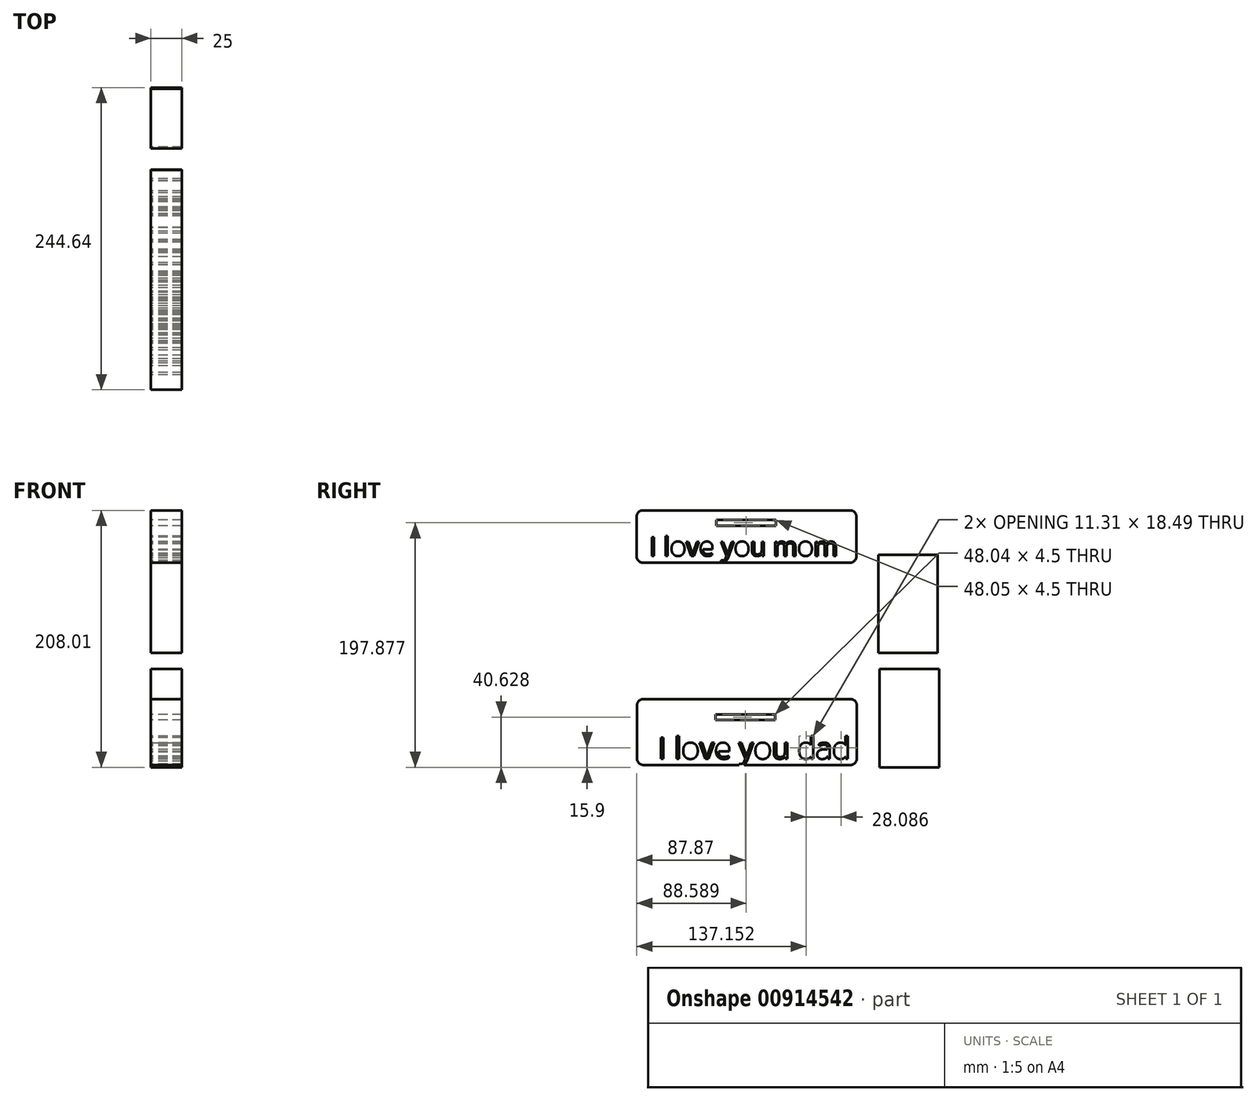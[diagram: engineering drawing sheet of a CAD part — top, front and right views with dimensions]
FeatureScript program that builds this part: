
annotation { "Feature Type Name" : "Feature", "Feature Type Description" : "" }
export const myFeature = defineFeature(function(context is Context, id is Id, definition is map)
    precondition{}
    {
        {
            var Q0;
            Q0=qCreatedBy(makeId("Right.planeOp"),FACE);
            var sketch = newSketch(context, id + "F0", { "sketchPlane" : qUnion([Q0])});
            skLineSegment(sketch, "E0", {"start": v(-72.6, 69.5) * mm, "end": v(66.76, 69.5) * mm});
            skLineSegment(sketch, "E1", {"start": v(71.76, 64.5) * mm, "end": v(71.76, 32.1) * mm});
            skLineSegment(sketch, "E2", {"start": v(66.76, 27.1) * mm, "end": v(-101.04, 27.1) * mm});
            skLineSegment(sketch, "E3", {"start": v(-106.04, 32.1) * mm, "end": v(-106.04, 64.5) * mm});
            skLineSegment(sketch, "E4", {"start": v(-101.04, 69.5) * mm, "end": v(-72.6, 69.5) * mm});
            skText(sketch, "E5", { "text": "I love you mom", "fontName": "OpenSans-Regular.ttf"});
            skLineSegment(sketch, "E6", {"start": v(89.45, 33.47) * mm, "end": v(137.5, 33.47) * mm});
            skLineSegment(sketch, "E7", {"start": v(137.5, 33.47) * mm, "end": v(137.5, -45.98) * mm});
            skLineSegment(sketch, "E8", {"start": v(137.5, -45.98) * mm, "end": v(89.45, -45.98) * mm});
            skLineSegment(sketch, "E9", {"start": v(89.45, -45.98) * mm, "end": v(89.45, 33.47) * mm});
            skPoint(sketch, "E10", {"position": v(-0.42, 69.5) * mm});
            skLineSegment(sketch, "E11", {"start": v(-41.47, 61.6) * mm, "end": v(6.57, 61.6) * mm});
            skLineSegment(sketch, "E12", {"start": v(6.57, 61.6) * mm, "end": v(6.57, 57.1) * mm});
            skLineSegment(sketch, "E13", {"start": v(6.57, 57.1) * mm, "end": v(-41.47, 57.1) * mm});
            skLineSegment(sketch, "E14", {"start": v(-41.47, 57.1) * mm, "end": v(-41.47, 61.6) * mm});
            skLineSegment(sketch, "E15", {"start": v(-106.17, -6.45) * mm, "end": v(-106.17, -6.45) * mm});
            skPoint(sketch, "E16.visualSharp", {"position": v(-106.04, 27.1) * mm});
            skArc(sketch, "E16.filletArc", {"start": v(-106.04, 32.1) * mm, "mid": v(-104.58, 28.57) * mm, "end": v(-101.04, 27.1) * mm});
            skPoint(sketch, "E17.visualSharp", {"position": v(71.76, 27.1) * mm});
            skArc(sketch, "E17.filletArc", {"start": v(66.76, 27.1) * mm, "mid": v(70.3, 28.57) * mm, "end": v(71.76, 32.1) * mm});
            skPoint(sketch, "E18.visualSharp", {"position": v(71.76, 69.5) * mm});
            skArc(sketch, "E18.filletArc", {"start": v(71.76, 64.5) * mm, "mid": v(70.3, 68.03) * mm, "end": v(66.76, 69.5) * mm});
            skPoint(sketch, "E19.visualSharp", {"position": v(-106.04, 69.5) * mm});
            skArc(sketch, "E19.filletArc", {"start": v(-101.04, 69.5) * mm, "mid": v(-104.58, 68.03) * mm, "end": v(-106.04, 64.5) * mm});
            skLineSegment(sketch, "E20", {"start": v(-105.73, -88.3) * mm, "end": v(-105.73, -131.63) * mm});
            skLineSegment(sketch, "E21", {"start": v(-100.73, -136.63) * mm, "end": v(67.07, -136.63) * mm});
            skLineSegment(sketch, "E22", {"start": v(72.07, -131.63) * mm, "end": v(72.07, -88.3) * mm});
            skLineSegment(sketch, "E23", {"start": v(67.07, -83.3) * mm, "end": v(-100.73, -83.3) * mm});
            skPoint(sketch, "E24.visualSharp", {"position": v(-105.73, -83.3) * mm});
            skArc(sketch, "E24.filletArc", {"start": v(-100.73, -83.3) * mm, "mid": v(-104.26, -84.75) * mm, "end": v(-105.73, -88.3) * mm});
            skPoint(sketch, "E25.visualSharp", {"position": v(-105.73, -136.63) * mm});
            skArc(sketch, "E25.filletArc", {"start": v(-105.73, -131.63) * mm, "mid": v(-104.26, -135.17) * mm, "end": v(-100.73, -136.63) * mm});
            skPoint(sketch, "E26.visualSharp", {"position": v(72.07, -136.63) * mm});
            skArc(sketch, "E26.filletArc", {"start": v(67.07, -136.63) * mm, "mid": v(70.6, -135.17) * mm, "end": v(72.07, -131.63) * mm});
            skPoint(sketch, "E27.visualSharp", {"position": v(72.07, -83.3) * mm});
            skArc(sketch, "E27.filletArc", {"start": v(72.07, -88.3) * mm, "mid": v(70.6, -84.75) * mm, "end": v(67.07, -83.3) * mm});
            skLineSegment(sketch, "E28", {"start": v(-42.2, -95.64) * mm, "end": v(-42.2, -100.14) * mm});
            skLineSegment(sketch, "E29", {"start": v(-42.2, -100.14) * mm, "end": v(5.85, -100.14) * mm});
            skLineSegment(sketch, "E30", {"start": v(5.85, -100.14) * mm, "end": v(5.85, -95.85) * mm});
            skLineSegment(sketch, "E31", {"start": v(5.85, -95.85) * mm, "end": v(-42.2, -95.64) * mm});
            skText(sketch, "E32", { "text": "I love you dad\n", "fontName": "OpenSans-Regular.ttf"});
            skLineSegment(sketch, "E33", {"start": v(90.56, -59.07) * mm, "end": v(90.56, -138.52) * mm});
            skLineSegment(sketch, "E34", {"start": v(90.56, -138.52) * mm, "end": v(138.6, -138.52) * mm});
            skLineSegment(sketch, "E35", {"start": v(138.6, -138.52) * mm, "end": v(138.6, -59.07) * mm});
            skLineSegment(sketch, "E36", {"start": v(138.6, -59.07) * mm, "end": v(90.56, -59.07) * mm});
            const initialGuessF0  = {"E5": [-0.09593, 0.03263, 1, 0, 0.01535], "E32": [-0.0888, -0.13163, 1, 0, 0.0173]};
            skSetInitialGuess(sketch, initialGuessF0);
            skSolve(sketch);
        }
        {
            var Q0;
            Q0=makeQuery(id+"F0.imprint","IMPRINT",FACE,{"disambiguationData":[TD([[makeQuery(id+"F0.imprint","IMPRINT",EDGE,{"derivedFrom":sQuery(id+"F0.wireOp",EDGE,"E6")}),-1.0]])]});
            var Q1;
            Q1=makeQuery(id+"F0.imprint","IMPRINT",FACE,{"disambiguationData":[TD([[makeQuery(id+"F0.imprint","IMPRINT",EDGE,{"derivedFrom":sQuery(id+"F0.wireOp",EDGE,"E20")}),1.0]])]});
            extrude(context, id + "F1", {"entities" : qUnion([Q0, Q1]), "depth" : 25 * mm, "offsetDistance" : 25 * mm});
        }
        {
            var Q0;
            Q0 = qSketchRegion(id + "F0", true);
            extrude(context, id + "F2", {"entities" : qUnion([Q0]), "depth" : 25 * mm, "offsetDistance" : 25 * mm});
        }
        {
            var Q0;
            Q0=makeQuery(id+"F2.opExtrude","SWEPT_BODY",BODY,{"disambiguationData":[OSD([sQuery(id+"F0.wireOp",EDGE,"E20"),sQuery(id+"F0.wireOp",EDGE,"E21"),sQuery(id+"F0.wireOp",EDGE,"E22"),sQuery(id+"F0.wireOp",EDGE,"E23"),sQuery(id+"F0.wireOp",EDGE,"E24.filletArc"),sQuery(id+"F0.wireOp",EDGE,"E25.filletArc"),sQuery(id+"F0.wireOp",EDGE,"E26.filletArc"),sQuery(id+"F0.wireOp",EDGE,"E27.filletArc"),sQuery(id+"F0.wireOp",EDGE,"E28"),sQuery(id+"F0.wireOp",EDGE,"E29"),sQuery(id+"F0.wireOp",EDGE,"E30"),sQuery(id+"F0.wireOp",EDGE,"E31"),sQuery(id+"F0.wireOp",EDGE,"E32.sketch_text.stroke-0"),sQuery(id+"F0.wireOp",EDGE,"E32.sketch_text.stroke-1"),sQuery(id+"F0.wireOp",EDGE,"E32.sketch_text.stroke-2"),sQuery(id+"F0.wireOp",EDGE,"E32.sketch_text.stroke-3"),sQuery(id+"F0.wireOp",EDGE,"E32.sketch_text.stroke-4"),sQuery(id+"F0.wireOp",EDGE,"E32.sketch_text.stroke-5"),sQuery(id+"F0.wireOp",EDGE,"E32.sketch_text.stroke-6"),sQuery(id+"F0.wireOp",EDGE,"E32.sketch_text.stroke-7"),sQuery(id+"F0.wireOp",EDGE,"E32.sketch_text.stroke-8"),sQuery(id+"F0.wireOp",EDGE,"E32.sketch_text.stroke-9"),sQuery(id+"F0.wireOp",EDGE,"E32.sketch_text.stroke-10"),sQuery(id+"F0.wireOp",EDGE,"E32.sketch_text.stroke-11"),sQuery(id+"F0.wireOp",EDGE,"E32.sketch_text.stroke-12"),sQuery(id+"F0.wireOp",EDGE,"E32.sketch_text.stroke-13"),sQuery(id+"F0.wireOp",EDGE,"E32.sketch_text.stroke-14"),sQuery(id+"F0.wireOp",EDGE,"E32.sketch_text.stroke-15"),sQuery(id+"F0.wireOp",EDGE,"E32.sketch_text.stroke-16"),sQuery(id+"F0.wireOp",EDGE,"E32.sketch_text.stroke-25"),sQuery(id+"F0.wireOp",EDGE,"E32.sketch_text.stroke-26"),sQuery(id+"F0.wireOp",EDGE,"E32.sketch_text.stroke-27"),sQuery(id+"F0.wireOp",EDGE,"E32.sketch_text.stroke-28"),sQuery(id+"F0.wireOp",EDGE,"E32.sketch_text.stroke-29"),sQuery(id+"F0.wireOp",EDGE,"E32.sketch_text.stroke-30"),sQuery(id+"F0.wireOp",EDGE,"E32.sketch_text.stroke-31"),sQuery(id+"F0.wireOp",EDGE,"E32.sketch_text.stroke-32"),sQuery(id+"F0.wireOp",EDGE,"E32.sketch_text.stroke-33"),sQuery(id+"F0.wireOp",EDGE,"E32.sketch_text.stroke-34"),sQuery(id+"F0.wireOp",EDGE,"E32.sketch_text.stroke-35"),sQuery(id+"F0.wireOp",EDGE,"E32.sketch_text.stroke-36"),sQuery(id+"F0.wireOp",EDGE,"E32.sketch_text.stroke-37"),sQuery(id+"F0.wireOp",EDGE,"E32.sketch_text.stroke-38"),sQuery(id+"F0.wireOp",EDGE,"E32.sketch_text.stroke-39"),sQuery(id+"F0.wireOp",EDGE,"E32.sketch_text.stroke-40"),sQuery(id+"F0.wireOp",EDGE,"E32.sketch_text.stroke-41"),sQuery(id+"F0.wireOp",EDGE,"E32.sketch_text.stroke-42"),sQuery(id+"F0.wireOp",EDGE,"E32.sketch_text.stroke-43"),sQuery(id+"F0.wireOp",EDGE,"E32.sketch_text.stroke-44"),sQuery(id+"F0.wireOp",EDGE,"E32.sketch_text.stroke-45"),sQuery(id+"F0.wireOp",EDGE,"E32.sketch_text.stroke-46"),sQuery(id+"F0.wireOp",EDGE,"E32.sketch_text.stroke-47"),sQuery(id+"F0.wireOp",EDGE,"E32.sketch_text.stroke-48"),sQuery(id+"F0.wireOp",EDGE,"E32.sketch_text.stroke-63"),sQuery(id+"F0.wireOp",EDGE,"E32.sketch_text.stroke-64"),sQuery(id+"F0.wireOp",EDGE,"E32.sketch_text.stroke-65"),sQuery(id+"F0.wireOp",EDGE,"E32.sketch_text.stroke-70"),sQuery(id+"F0.wireOp",EDGE,"E32.sketch_text.stroke-71"),sQuery(id+"F0.wireOp",EDGE,"E32.sketch_text.stroke-72"),sQuery(id+"F0.wireOp",EDGE,"E32.sketch_text.stroke-73"),sQuery(id+"F0.wireOp",EDGE,"E32.sketch_text.stroke-74"),sQuery(id+"F0.wireOp",EDGE,"E32.sketch_text.stroke-75"),sQuery(id+"F0.wireOp",EDGE,"E32.sketch_text.stroke-76"),sQuery(id+"F0.wireOp",EDGE,"E32.sketch_text.stroke-77"),sQuery(id+"F0.wireOp",EDGE,"E32.sketch_text.stroke-78"),sQuery(id+"F0.wireOp",EDGE,"E32.sketch_text.stroke-87"),sQuery(id+"F0.wireOp",EDGE,"E32.sketch_text.stroke-88"),sQuery(id+"F0.wireOp",EDGE,"E32.sketch_text.stroke-89"),sQuery(id+"F0.wireOp",EDGE,"E32.sketch_text.stroke-90"),sQuery(id+"F0.wireOp",EDGE,"E32.sketch_text.stroke-91"),sQuery(id+"F0.wireOp",EDGE,"E32.sketch_text.stroke-92"),sQuery(id+"F0.wireOp",EDGE,"E32.sketch_text.stroke-93"),sQuery(id+"F0.wireOp",EDGE,"E32.sketch_text.stroke-94"),sQuery(id+"F0.wireOp",EDGE,"E32.sketch_text.stroke-95"),sQuery(id+"F0.wireOp",EDGE,"E32.sketch_text.stroke-96"),sQuery(id+"F0.wireOp",EDGE,"E32.sketch_text.stroke-97"),sQuery(id+"F0.wireOp",EDGE,"E32.sketch_text.stroke-98"),sQuery(id+"F0.wireOp",EDGE,"E32.sketch_text.stroke-99"),sQuery(id+"F0.wireOp",EDGE,"E32.sketch_text.stroke-100"),sQuery(id+"F0.wireOp",EDGE,"E32.sketch_text.stroke-101"),sQuery(id+"F0.wireOp",EDGE,"E32.sketch_text.stroke-102"),sQuery(id+"F0.wireOp",EDGE,"E32.sketch_text.stroke-103"),sQuery(id+"F0.wireOp",EDGE,"E32.sketch_text.stroke-104"),sQuery(id+"F0.wireOp",EDGE,"E32.sketch_text.stroke-105"),sQuery(id+"F0.wireOp",EDGE,"E32.sketch_text.stroke-106"),sQuery(id+"F0.wireOp",EDGE,"E32.sketch_text.stroke-107"),sQuery(id+"F0.wireOp",EDGE,"E32.sketch_text.stroke-108"),sQuery(id+"F0.wireOp",EDGE,"E32.sketch_text.stroke-109"),sQuery(id+"F0.wireOp",EDGE,"E32.sketch_text.stroke-110"),sQuery(id+"F0.wireOp",EDGE,"E32.sketch_text.stroke-111"),sQuery(id+"F0.wireOp",EDGE,"E32.sketch_text.stroke-112"),sQuery(id+"F0.wireOp",EDGE,"E32.sketch_text.stroke-113"),sQuery(id+"F0.wireOp",EDGE,"E32.sketch_text.stroke-114"),sQuery(id+"F0.wireOp",EDGE,"E32.sketch_text.stroke-115"),sQuery(id+"F0.wireOp",EDGE,"E32.sketch_text.stroke-116"),sQuery(id+"F0.wireOp",EDGE,"E32.sketch_text.stroke-117"),sQuery(id+"F0.wireOp",EDGE,"E32.sketch_text.stroke-118"),sQuery(id+"F0.wireOp",EDGE,"E32.sketch_text.stroke-128"),sQuery(id+"F0.wireOp",EDGE,"E32.sketch_text.stroke-129"),sQuery(id+"F0.wireOp",EDGE,"E32.sketch_text.stroke-130"),sQuery(id+"F0.wireOp",EDGE,"E32.sketch_text.stroke-131"),sQuery(id+"F0.wireOp",EDGE,"E32.sketch_text.stroke-132"),sQuery(id+"F0.wireOp",EDGE,"E32.sketch_text.stroke-133"),sQuery(id+"F0.wireOp",EDGE,"E32.sketch_text.stroke-134"),sQuery(id+"F0.wireOp",EDGE,"E32.sketch_text.stroke-135"),sQuery(id+"F0.wireOp",EDGE,"E32.sketch_text.stroke-136"),sQuery(id+"F0.wireOp",EDGE,"E32.sketch_text.stroke-137"),sQuery(id+"F0.wireOp",EDGE,"E32.sketch_text.stroke-138"),sQuery(id+"F0.wireOp",EDGE,"E32.sketch_text.stroke-139"),sQuery(id+"F0.wireOp",EDGE,"E32.sketch_text.stroke-140"),sQuery(id+"F0.wireOp",EDGE,"E32.sketch_text.stroke-141"),sQuery(id+"F0.wireOp",EDGE,"E32.sketch_text.stroke-142"),sQuery(id+"F0.wireOp",EDGE,"E32.sketch_text.stroke-143"),sQuery(id+"F0.wireOp",EDGE,"E32.sketch_text.stroke-144"),sQuery(id+"F0.wireOp",EDGE,"E32.sketch_text.stroke-145"),sQuery(id+"F0.wireOp",EDGE,"E32.sketch_text.stroke-146"),sQuery(id+"F0.wireOp",EDGE,"E32.sketch_text.stroke-155"),sQuery(id+"F0.wireOp",EDGE,"E32.sketch_text.stroke-156"),sQuery(id+"F0.wireOp",EDGE,"E32.sketch_text.stroke-157"),sQuery(id+"F0.wireOp",EDGE,"E32.sketch_text.stroke-158"),sQuery(id+"F0.wireOp",EDGE,"E32.sketch_text.stroke-159"),sQuery(id+"F0.wireOp",EDGE,"E32.sketch_text.stroke-160"),sQuery(id+"F0.wireOp",EDGE,"E32.sketch_text.stroke-161"),sQuery(id+"F0.wireOp",EDGE,"E32.sketch_text.stroke-162"),sQuery(id+"F0.wireOp",EDGE,"E32.sketch_text.stroke-163"),sQuery(id+"F0.wireOp",EDGE,"E32.sketch_text.stroke-164"),sQuery(id+"F0.wireOp",EDGE,"E32.sketch_text.stroke-165"),sQuery(id+"F0.wireOp",EDGE,"E32.sketch_text.stroke-166"),sQuery(id+"F0.wireOp",EDGE,"E32.sketch_text.stroke-167"),sQuery(id+"F0.wireOp",EDGE,"E32.sketch_text.stroke-168"),sQuery(id+"F0.wireOp",EDGE,"E32.sketch_text.stroke-169")])]});
            deleteBodies(context, id + "F3", {"entities" : qUnion([Q0])});
        }
    });
